# Revit family: QF_BPRO_SW 6x4 - 3_569768
name_source: partatom
category: Sonderausstattung
revit_build: Autodesk Revit 2018 (Build: 20190510_1515(x64)
units: mm (PartAtom-declared; Revit-internal decimal feet)

## family parameters
Arbeitsebenenbasiert = Nein
Beim Laden mit Abzugskörper schneiden = Nein
Bemaßung runder Anschluss = Durchmesser verwenden
Gemeinsam genutzt = Nein
Immer vertikal = Ja
Raumberechnungspunkt = Nein
Teiletyp = Normal

## types (1)
- SW 6x4 - 3
    Artikel Nummer = 569768
    Beschreibung = Servierwagen aus rostfreiem Edelstahl
mit 3 Borden 600 x 400 mm
max. Belastung je Bord: 80 kg
Tragfähigkeit: 120 kg
    Beschreibung durch Hersteller analog Leistungsverzeichniskurztext = Abmessungen

Länge:				700 mm
Breite:			500 mm
Höhe:			950 mm

Lichtes Maß:
Höhe zwischen den Borden:	275 mm
Borde:		 600 x 400 mm

Ausführung

Der Servierwagen besteht aus CNS 18/10, Werkstoff-Nr. 1.4301. Zwischen stabilem Rundrohr mit D = 25 mm befinden sich drei eingeschweißte tiefgezogene Borde. Die Oberfläche der Borde ist mikroliert. Die Rundrohre an den Stirnseiten werden als Schiebegriffe genutzt. Ein umlaufender 35 mm abgekanteter Profilrand an den Borden, die Rollierung der Bordkante sowie durchgehende Schweißnähte zwischen Rohrrahmen und Borden verstärken die Stabilität des Servierwagens.
Die Borde sind mit einer schalldämmenden Antidröhnmatte unterfüttert.

Der Servierwagen ist fahrbar mittels rostfreien Kunststoffrollen gemäß DIN 18867, Teil 8 (4 Lenkrollen, davon 2 mit Feststeller, Rollendurchmesser 125 mm). Die Rollen sind im Rohrrahmen eingesteckt. Wandabweiser aus Kunststoff (Polyethylen) an allen vier Ecken schützen vor Beschädigung.


Zubehör/ Optionen

•	Besteckbehälter BGN 1/3-150 aus CNS, mit Hängevorrichtung, 110 Besteckteile 
(Best.Nr. 555 510)
•	Galerie umlaufend, 50 mm hoch 
•	Knotenbleche zur Stärkung der Stabiliät
•	Luftidentische Rollen, 4 Lenkrollen, davon 2 mit Feststeller, Durchmesser 125 mm





Technische Daten

Werkstoff:	Chromnickelstahl 18/10,
		Polyamid (PA)
Gewicht:		12,66 kg
Tragfähigkeit je Wagen:	120 kg
Tragfähigkeit je Bord:	80 kg
Anzahl der Borde:		 3


Besonderheit

•	Umlaufender Profilrand an den Borden zur Verstärkung der Stabilität des Servierwagens und Verhinderung von seitlichem Abrutschen der abgestellten Gegenstände

•	Rollierung der Bordkante: eingerollte Kanten sorgen für hohe Stabilität und schützen das Personal vor Verletzungen.


Fabrikat

Hersteller:	B.PRO
Typ:                                      SW 6x4-3
Best.Nr.		569 768
    Beschreibung durch Hersteller analog Leistungsverzeichnislangtext = Abmessungen

Länge:				700 mm
Breite:			500 mm
Höhe:			950 mm

Lichtes Maß:
Höhe zwischen den Borden:	275 mm
Borde:		 600 x 400 mm

Ausführung

Der Servierwagen besteht aus CNS 18/10, Werkstoff-Nr. 1.4301. Zwischen stabilem Rundrohr mit D = 25 mm befinden sich drei eingeschweißte tiefgezogene Borde. Die Oberfläche der Borde ist mikroliert. Die Rundrohre an den Stirnseiten werden als Schiebegriffe genutzt. Ein umlaufender 35 mm abgekanteter Profilrand an den Borden, die Rollierung der Bordkante sowie durchgehende Schweißnähte zwischen Rohrrahmen und Borden verstärken die Stabilität des Servierwagens.
Die Borde sind mit einer schalldämmenden Antidröhnmatte unterfüttert.

Der Servierwagen ist fahrbar mittels rostfreien Kunststoffrollen gemäß DIN 18867, Teil 8 (4 Lenkrollen, davon 2 mit Feststeller, Rollendurchmesser 125 mm). Die Rollen sind im Rohrrahmen eingesteckt. Wandabweiser aus Kunststoff (Polyethylen) an allen vier Ecken schützen vor Beschädigung.


Zubehör/ Optionen

•	Besteckbehälter BGN 1/3-150 aus CNS, mit Hängevorrichtung, 110 Besteckteile 
(Best.Nr. 555 510)
•	Galerie umlaufend, 50 mm hoch 
•	Knotenbleche zur Stärkung der Stabiliät
•	Luftidentische Rollen, 4 Lenkrollen, davon 2 mit Feststeller, Durchmesser 125 mm





Technische Daten

Werkstoff:	Chromnickelstahl 18/10,
		Polyamid (PA)
Gewicht:		12,66 kg
Tragfähigkeit je Wagen:	120 kg
Tragfähigkeit je Bord:	80 kg
Anzahl der Borde:		 3


Besonderheit

•	Umlaufender Profilrand an den Borden zur Verstärkung der Stabilität des Servierwagens und Verhinderung von seitlichem Abrutschen der abgestellten Gegenstände

•	Rollierung der Bordkante: eingerollte Kanten sorgen für hohe Stabilität und schützen das Personal vor Verletzungen.


Fabrikat

Hersteller:	B.PRO
Typ:                                      SW 6x4-3
Best.Nr.		569 768
    Breite Korpus = 400 mm  [stored 1.31234 ft]
    Gerätegewicht Netto = 12.66 kg
    Großküchengerätezuordnung = Ja
    Hersteller = B.PRO GmbH
    Höhe = 950 mm  [stored 3.1168 ft]
    Höhe2 = 938 mm
    Internetadresse Gerätehersteller = https://www.bpro-solutions.com
    Internetadresse für Ersatzteilliste = https://www.bpro-solutions.com
    Kosten = 323.3 $
    Länge Gerätebreite = 700 mm  [stored 2.29659 ft]
    Länge Korpus = 600 mm  [stored 1.9685 ft]
    Material = QF_Metal-Stainless-Steel_general
    Material_Stoßschutz = QF_Rubber-Black-Matt
    Modell = SW 6 x 4-3
    Sockelhöhe = 180 mm  [stored 0.590551 ft]
    Tiefe = 500 mm  [stored 1.64042 ft]
    Typenkommentare = Servierwagen 6 x 4-3
    URL = https://www.bpro-solutions.com
    Warnhinweise = Ausführliche Gefahrenhinweise entnehmen Sie der Betriebsanleitung.
    Zubehör = Nein

note: [stored X ft] marks values corroborated as IEEE doubles in the binary element streams (Revit-internal decimal feet)
